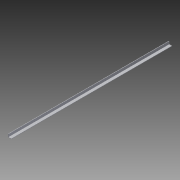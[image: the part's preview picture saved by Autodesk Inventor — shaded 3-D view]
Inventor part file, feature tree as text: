
AUTODESK INVENTOR PART (.ipt)
format: ipt  version: 2013 (Build 170138000, 138)  size: 76,800 bytes
history: native  units: in
note: dims shown in document units (in); Inventor stores cm internally (conversion verified against a paired STEP export)
features: extrude x1, sketch x1
ambient origin geometry x8: Origin, YZ Plane, XZ Plane, XY Plane, X Axis, Y Axis, Z Axis, Center Point
bodies: Solid1 (feature_tree)
feature tree (2):
  extrude  "Extrusion1"  Depth=0.0625in
  sketch  "Sketch1"  dims[d0=0.5in d1=0.0625in d2=0.5in d3=0.0625in d4=25.75in d5=0.0in]
